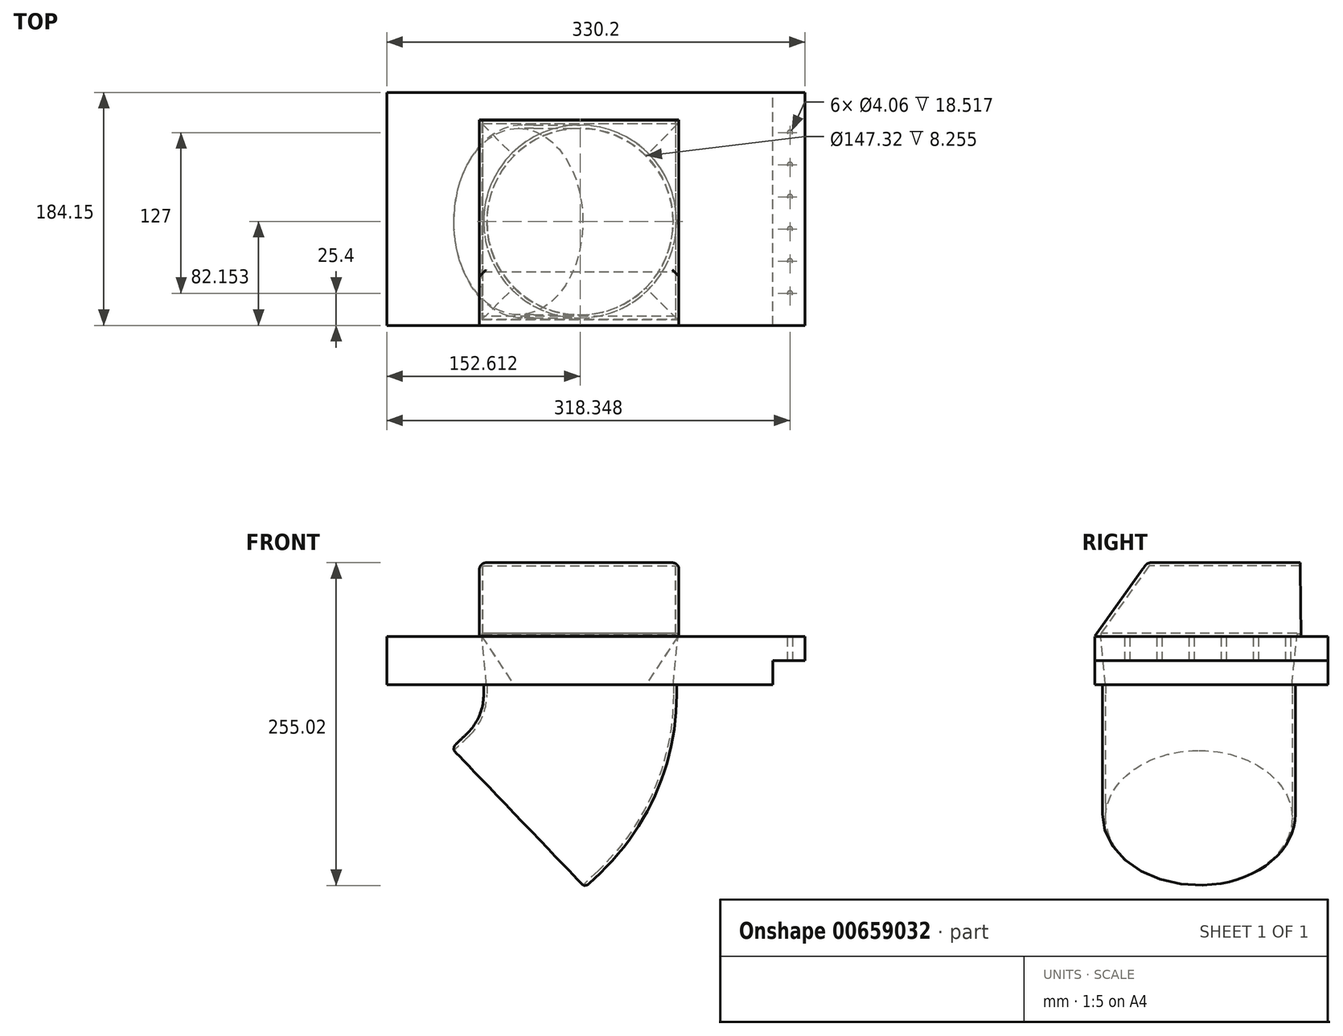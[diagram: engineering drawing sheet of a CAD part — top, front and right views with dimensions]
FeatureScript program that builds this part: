
annotation { "Feature Type Name" : "Feature", "Feature Type Description" : "" }
export const myFeature = defineFeature(function(context is Context, id is Id, definition is map)
    precondition{}
    {
        {
            var Q0;
            Q0=qCreatedBy(makeId("Front.planeOp"),FACE);
            var sketch = newSketch(context, id + "F0", { "sketchPlane" : qUnion([Q0])});
            skLineSegment(sketch, "E0.bottom", {"start": v(0, 0) * mm, "end": v(-304.8, 0) * mm});
            skLineSegment(sketch, "E0.top", {"start": v(0, 38.1) * mm, "end": v(-304.8, 38.1) * mm});
            skLineSegment(sketch, "E0.left", {"start": v(0, 0) * mm, "end": v(0, 38.1) * mm});
            skLineSegment(sketch, "E0.right", {"start": v(-304.8, 0) * mm, "end": v(-304.8, 38.1) * mm});
            skSolve(sketch);
        }
        {
            var Q0;
            Q0=makeQuery(id+"F0.imprint","IMPRINT",FACE,{"disambiguationData":[TD([[makeQuery(id+"F0.imprint","IMPRINT",EDGE,{"derivedFrom":sQuery(id+"F0.wireOp",EDGE,"E0.bottom")}),-1.0]])]});
            extrude(context, id + "F1", {"entities" : qUnion([Q0]), "depth" : 184.15 * mm, "offsetDistance" : 25.4 * mm});
        }
        {
            var Q0;
            Q0=makeQuery(id+"F1.opExtrude","SWEPT_FACE",FACE,{"disambiguationData":[OSD([sQuery(id+"F0.wireOp",EDGE,"E0.bottom")])]});
            var sketch = newSketch(context, id + "F2", { "sketchPlane" : qUnion([Q0])});
            skLineSegment(sketch, "E1", {"start": v(-304.8, 25.4) * mm, "end": v(0, 25.4) * mm, "construction": true});
            skLineSegment(sketch, "E2", {"start": v(-152.4, 0) * mm, "end": v(-152.4, 184.15) * mm, "construction": true});
            skCircle(sketch, "E3", {"center": v(-152.4, 102.27) * mm, "radius": 73.66 * mm});
            skSolve(sketch);
        }
        {
            var Q0;
            Q0=makeQuery(id+"F1.opExtrude","SWEPT_FACE",FACE,{"disambiguationData":[OSD([sQuery(id+"F0.wireOp",EDGE,"E0.top")])]});
            var sketch = newSketch(context, id + "F3", { "sketchPlane" : qUnion([Q0])});
            skLineSegment(sketch, "E4.bottom", {"start": v(-229.83, -24.64) * mm, "end": v(-74.9, -24.64) * mm});
            skLineSegment(sketch, "E4.top", {"start": v(-229.83, -179.58) * mm, "end": v(-74.9, -179.58) * mm});
            skLineSegment(sketch, "E4.left", {"start": v(-229.83, -24.64) * mm, "end": v(-229.83, -179.58) * mm});
            skLineSegment(sketch, "E4.right", {"start": v(-74.9, -24.64) * mm, "end": v(-74.9, -179.58) * mm});
            skSolve(sketch);
        }
        {
            var Q0;
            Q0=qCreatedBy(makeId("Right.planeOp"),FACE);
            cPlane(context, id + "F4", {"entities" : qUnion([Q0]), "cplaneType" : CPlaneType.OFFSET, "offset" : 74.17 * mm, "oppositeDirection" : true, "width" : 152.4 * mm, "height" : 152.4 * mm});
        }
        {
            var Q0;
            Q0=qCreatedBy(id+"F4.planeOp",FACE);
            var sketch = newSketch(context, id + "F5", { "sketchPlane" : qUnion([Q0])});
            skLineSegment(sketch, "E5", {"start": v(-21.5, 37.62) * mm, "end": v(-21.85, 96.32) * mm});
            skLineSegment(sketch, "E6", {"start": v(-21.85, 96.32) * mm, "end": v(-142.8, 96.32) * mm});
            skLineSegment(sketch, "E7", {"start": v(-142.8, 96.32) * mm, "end": v(-184.14, 38.21) * mm});
            skLineSegment(sketch, "E8", {"start": v(-184.14, 38.21) * mm, "end": v(-21.5, 37.62) * mm});
            skSolve(sketch);
        }
        {
            var Q0;
            Q0=qSketchRegion(id+"F5",true);
            extrude(context, id + "F6", {"entities" : qUnion([Q0]), "operationType" : NewBodyOperationType.ADD, "oppositeDirection" : true, "depth" : 157.48 * mm, "offsetDistance" : 25.4 * mm});
        }
        {
            var Q0;
            Q0=makeQuery(id+"F6.opExtrude","SWEPT_FACE",FACE,{"disambiguationData":[OSD([sQuery(id+"F5.wireOp",EDGE,"E5")])]});
            shell(context, id + "F7", {"entities" : qUnion([Q0]), "thickness" : 2.54 * mm});
        }
        {
            var Q1;
            Q1=qSketchRegion(id+"F3",true);
            var Q2;
            Q2=qSketchRegion(id+"F2",true);
            loft(context, id + "F8", {"operationType" : NewBodyOperationType.REMOVE, "sheetProfilesArray" : [{ "sheetProfileEntities" : qUnion([Q1]) }, { "sheetProfileEntities" : qUnion([Q2]) }]});
        }
        {
            var Q0;
            Q0=qSketchRegion(id+"F3",true);
            extrude(context, id + "F9", {"entities" : qUnion([Q0]), "operationType" : NewBodyOperationType.REMOVE, "depth" : 2.62 * mm, "offsetDistance" : 25.4 * mm});
        }
        {
            var Q0;
            Q0=qCreatedBy(makeId("Front.planeOp"),FACE);
            cPlane(context, id + "F10", {"entities" : qUnion([Q0]), "cplaneType" : CPlaneType.OFFSET, "offset" : 102.36 * mm, "width" : 152.4 * mm, "height" : 152.4 * mm});
        }
        {
            var Q0;
            Q0=qCreatedBy(id+"F10.planeOp",FACE);
            var sketch = newSketch(context, id + "F11", { "sketchPlane" : qUnion([Q0])});
            skLineSegment(sketch, "E9", {"start": v(-74.86, 0) * mm, "end": v(-228.5, 0) * mm, "construction": true});
            skLineSegment(sketch, "E10", {"start": v(-151.68, 0) * mm, "end": v(-151.68, -7.91) * mm});
            skPoint(sketch, "E11.visualSharp", {"position": v(-151.68, -76.2) * mm});
            skArc(sketch, "E12", {"start": v(-188.52, -94.16) * mm, "mid": v(-161.27, -54.8) * mm, "end": v(-151.68, -7.91) * mm});
            skLineSegment(sketch, "E13", {"start": v(-188.52, -94.16) * mm, "end": v(-200.52, -105.65) * mm});
            skLineSegment(sketch, "E14", {"start": v(-151.68, 0) * mm, "end": v(-151.68, 0.34) * mm});
            skSolve(sketch);
        }
        {
            var Q0;
            Q0=makeQuery(id+"F1.opExtrude","SWEPT_FACE",FACE,{"disambiguationData":[OSD([sQuery(id+"F0.wireOp",EDGE,"E0.bottom")])]});
            var sketch = newSketch(context, id + "F12", { "sketchPlane" : qUnion([Q0])});
            skCircle(sketch, "E15", {"center": v(-152.19, 102) * mm, "radius": 76.2 * mm});
            skSolve(sketch);
        }
        {
            var Q0;
            Q0 = qSketchRegion(id + "F12", true);
            var Q1;
            Q1=qConstructionFilter(qBodyType(qCreatedBy(id+"F11",EDGE),BodyType.WIRE),ConstructionObject.NO);
            sweep(context, id + "F13", {"profiles" : qUnion([Q0]), "path" : qUnion([Q1])});
        }
        {
            var Q0;
            Q0=makeQuery(id+"F13.opSweep","CAP_FACE",FACE,{"disambiguationData":[OSD([sQuery(id+"F11.wireOp",VERTEX,"E14.end"),sQuery(id+"F12.wireOp",EDGE,"E15")])],"isStart":true});
            var Q1;
            Q1=makeQuery(id+"F13.opSweep","CAP_FACE",FACE,{"disambiguationData":[OSD([sQuery(id+"F11.wireOp",VERTEX,"E13.end"),sQuery(id+"F12.wireOp",EDGE,"E15")])],"isStart":false});
            var Q2;
            Q2=makeQuery(id+"F13.opSweep","SWEPT_BODY",BODY,{"disambiguationData":[OSD([sQuery(id+"F2.wireOp",EDGE,"E3"),sQuery(id+"F11.wireOp",EDGE,"E10")])]});
            shell(context, id + "F14", {"entities" : qUnion([Q0, Q1]), "parts" : qUnion([Q2]), "thickness" : 2.54 * mm});
        }
        {
            var Q0;
            Q0=makeQuery(id+"F6.opExtrude","CAP_EDGE",EDGE,{"disambiguationData":[OSD([sQuery(id+"F5.wireOp",EDGE,"E6")])],"isStart":true});
            var Q1;
            Q1=makeQuery(id+"F6.opExtrude","SWEPT_EDGE",EDGE,{"disambiguationData":[OSD([sQuery(id+"F5.wireOp",EDGE,"E6"),sQuery(id+"F5.wireOp",EDGE,"E7")])]});
            var Q2;
            Q2=makeQuery(id+"F6.opExtrude","CAP_EDGE",EDGE,{"disambiguationData":[OSD([sQuery(id+"F5.wireOp",EDGE,"E6")])],"isStart":false});
            fillet(context, id + "F15", {"entities" : qUnion([Q0, Q1, Q2]), "radius" : 5.08 * mm, "tangentPropagation" : true, "allowEdgeOverflow" : false});
        }
        {
            var Q0;
            Q0=makeQuery(id+"F13.opSweep","CAP_EDGE",EDGE,{"disambiguationData":[OSD([sQuery(id+"F11.wireOp",VERTEX,"E13.end"),sQuery(id+"F12.wireOp",EDGE,"E15")])],"isStart":false});
            fillet(context, id + "F16", {"entities" : qUnion([Q0]), "radius" : 5.08 * mm, "tangentPropagation" : true, "allowEdgeOverflow" : false});
        }
        {
            var Q0;
            Q0=makeQuery(id+"F1.opExtrude","SWEPT_FACE",FACE,{"disambiguationData":[OSD([sQuery(id+"F0.wireOp",EDGE,"E0.left")])]});
            var sketch = newSketch(context, id + "F17", { "sketchPlane" : qUnion([Q0])});
            skLineSegment(sketch, "E16.bottom", {"start": v(-184.15, 38.1) * mm, "end": v(0, 38.1) * mm});
            skLineSegment(sketch, "E16.top", {"start": v(-184.15, 19.05) * mm, "end": v(0, 19.05) * mm});
            skLineSegment(sketch, "E16.left", {"start": v(-184.15, 38.1) * mm, "end": v(-184.15, 19.05) * mm});
            skLineSegment(sketch, "E16.right", {"start": v(0, 38.1) * mm, "end": v(0, 19.05) * mm});
            skSolve(sketch);
        }
        {
            var Q0;
            Q0=makeQuery(id+"F17.imprint","IMPRINT",FACE,{"disambiguationData":[TD([[makeQuery(id+"F17.imprint","IMPRINT",EDGE,{"derivedFrom":sQuery(id+"F17.wireOp",EDGE,"E16.bottom")}),-1.0]])]});
            extrude(context, id + "F18", {"entities" : qUnion([Q0]), "operationType" : NewBodyOperationType.ADD, "depth" : 25.4 * mm, "offsetDistance" : 25.4 * mm});
        }
        {
            var Q0;
            Q0=makeQuery(id+"F18.opExtrude","SWEPT_FACE",FACE,{"disambiguationData":[OSD([sQuery(id+"F17.wireOp",EDGE,"E16.top")])]});
            var sketch = newSketch(context, id + "F19", { "sketchPlane" : qUnion([Q0])});
            skCircle(sketch, "E17", {"center": v(13.55, 158.75) * mm, "radius": 2.03 * mm});
            skCircle(sketch, "E18.0.1.0", {"center": v(13.55, 133.35) * mm, "radius": 2.03 * mm});
            skCircle(sketch, "E18.0.2.0", {"center": v(13.55, 107.95) * mm, "radius": 2.03 * mm});
            skCircle(sketch, "E18.0.3.0", {"center": v(13.55, 82.55) * mm, "radius": 2.03 * mm});
            skCircle(sketch, "E18.0.4.0", {"center": v(13.55, 57.15) * mm, "radius": 2.03 * mm});
            skCircle(sketch, "E18.0.5.0", {"center": v(13.55, 31.75) * mm, "radius": 2.03 * mm});
            skLineSegment(sketch, "E18.direction1", {"start": v(13.55, 158.75) * mm, "end": v(38.95, 158.75) * mm, "construction": true});
            skLineSegment(sketch, "E18.direction2", {"start": v(13.55, 158.75) * mm, "end": v(13.55, 133.35) * mm, "construction": true});
            skSolve(sketch);
        }
        {
            var Q0;
            Q0=qSketchRegion(id+"F19",true);
            extrude(context, id + "F20", {"entities" : qUnion([Q0]), "operationType" : NewBodyOperationType.REMOVE, "oppositeDirection" : true, "depth" : 18.52 * mm, "offsetDistance" : 25.4 * mm});
        }
    });
